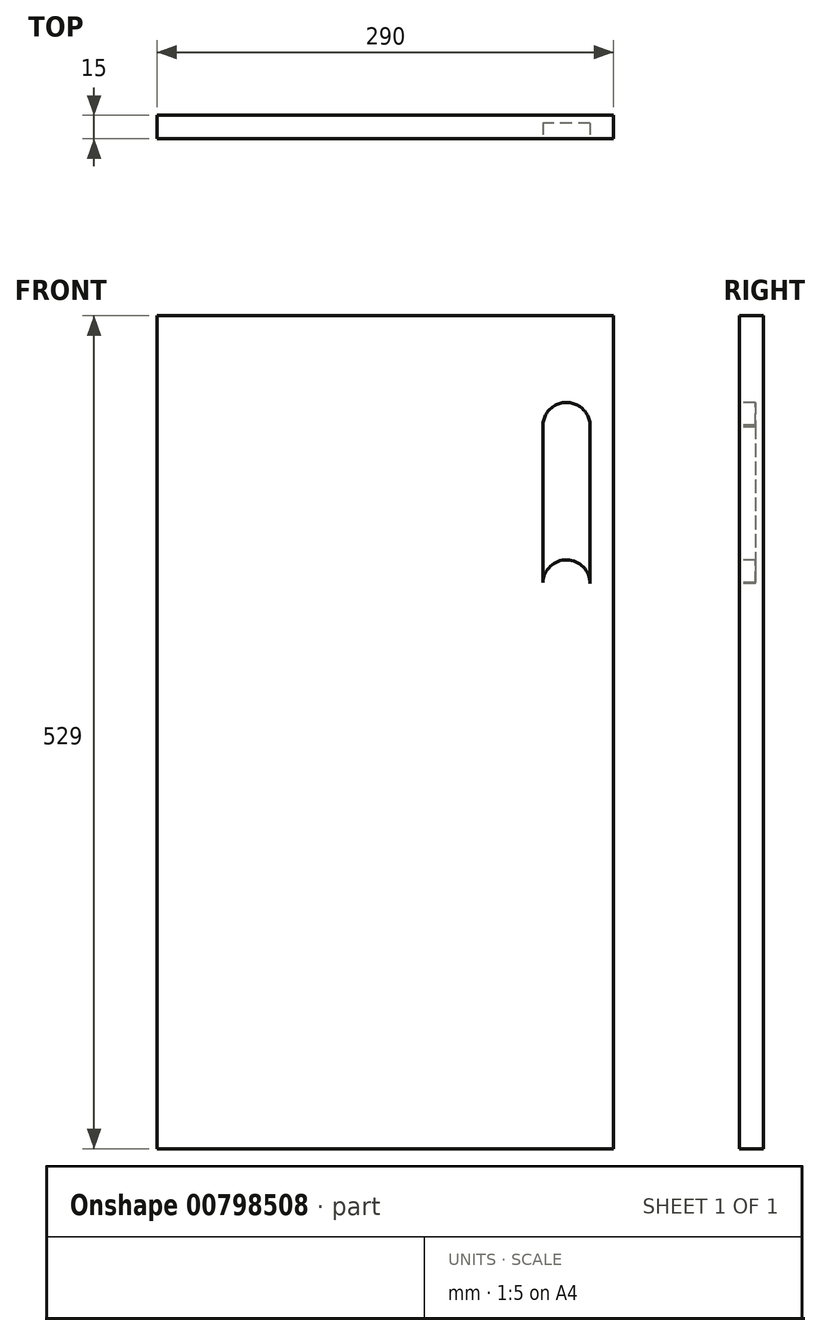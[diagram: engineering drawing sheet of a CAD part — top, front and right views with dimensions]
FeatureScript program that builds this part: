
annotation { "Feature Type Name" : "Feature", "Feature Type Description" : "" }
export const myFeature = defineFeature(function(context is Context, id is Id, definition is map)
    precondition{}
    {
        {
            var Q0;
            Q0=qCreatedBy(makeId("Front.planeOp"),FACE);
            var sketch = newSketch(context, id + "F0", { "sketchPlane" : qUnion([Q0])});
            skLineSegment(sketch, "E0.bottom", {"start": v(0, 0) * mm, "end": v(290, 0) * mm});
            skLineSegment(sketch, "E0.top", {"start": v(0, -529) * mm, "end": v(290, -529) * mm});
            skLineSegment(sketch, "E0.left", {"start": v(0, 0) * mm, "end": v(0, -529) * mm});
            skLineSegment(sketch, "E0.right", {"start": v(290, 0) * mm, "end": v(290, -529) * mm});
            skSolve(sketch);
        }
        {
            var Q0;
            Q0=makeQuery(id+"F0.imprint","IMPRINT",FACE,{"disambiguationData":[TD([[makeQuery(id+"F0.imprint","IMPRINT",EDGE,{"derivedFrom":sQuery(id+"F0.wireOp",EDGE,"E0.bottom")}),-1.0]])]});
            extrude(context, id + "F1", {"entities" : qUnion([Q0]), "depth" : 15 * mm, "offsetDistance" : 25 * mm});
        }
        {
            var Q0;
            Q0=makeQuery(id+"F1.opExtrude","CAP_FACE",FACE,{"disambiguationData":[OSD([sQuery(id+"F0.wireOp",EDGE,"E0.bottom"),sQuery(id+"F0.wireOp",EDGE,"E0.top"),sQuery(id+"F0.wireOp",EDGE,"E0.left"),sQuery(id+"F0.wireOp",EDGE,"E0.right")])],"isStart":false});
            var sketch = newSketch(context, id + "F2", { "sketchPlane" : qUnion([Q0])});
            skCircle(sketch, "E1", {"center": v(260, -170) * mm, "radius": 15 * mm});
            skCircle(sketch, "E2", {"center": v(260, -70) * mm, "radius": 15 * mm});
            skLineSegment(sketch, "E3", {"start": v(245.01, -70.64) * mm, "end": v(245.01, -170.64) * mm});
            skLineSegment(sketch, "E4", {"start": v(275, -69.51) * mm, "end": v(275, -170.64) * mm});
            skSolve(sketch);
        }
        {
            var Q0;
            {var subQ0=sQuery(id+"F2.wireOp",EDGE,"E4");var subQ1=sQuery(id+"F2.wireOp",EDGE,"E1");var subQ2=makeQuery(id+"F2.imprint","INTERSECT",VERTEX,{"derivedFrom":[subQ1,subQ0]});Q0=makeQuery(id+"F2.imprint","IMPRINT",FACE,{"disambiguationData":[TD([[makeQuery(id+"F2.imprint","IMPRINT",EDGE,{"disambiguationData":[TD([[subQ2,-1.0]])],"derivedFrom":subQ1}),-1.0]])]});}
            var Q1;
            {var subQ0=sQuery(id+"F2.wireOp",EDGE,"E2");var subQ1=makeQuery(id+"F2.imprint","INTERSECT",VERTEX,{"derivedFrom":[subQ0,sQuery(id+"F2.wireOp",EDGE,"E3")]});Q1=makeQuery(id+"F2.imprint","IMPRINT",FACE,{"disambiguationData":[TD([[makeQuery(id+"F2.imprint","IMPRINT",EDGE,{"disambiguationData":[TD([[subQ1,1.0]])],"derivedFrom":subQ0}),1.0]])]});}
            var Q2;
            {var subQ0=sQuery(id+"F2.wireOp",EDGE,"E1");var subQ1=makeQuery(id+"F2.imprint","IMPRINT",VERTEX,{"derivedFrom":subQ0});Q2=makeQuery(id+"F2.imprint","IMPRINT",FACE,{"disambiguationData":[TD([[makeQuery(id+"F2.imprint","IMPRINT",EDGE,{"disambiguationData":[TD([[subQ1,-1.0]])],"derivedFrom":subQ0}),1.0]])]});}
            extrude(context, id + "F3", {"entities" : qUnion([Q0, Q1, Q2]), "operationType" : NewBodyOperationType.REMOVE, "oppositeDirection" : true, "depth" : 10 * mm, "offsetDistance" : 25 * mm});
        }
    });
